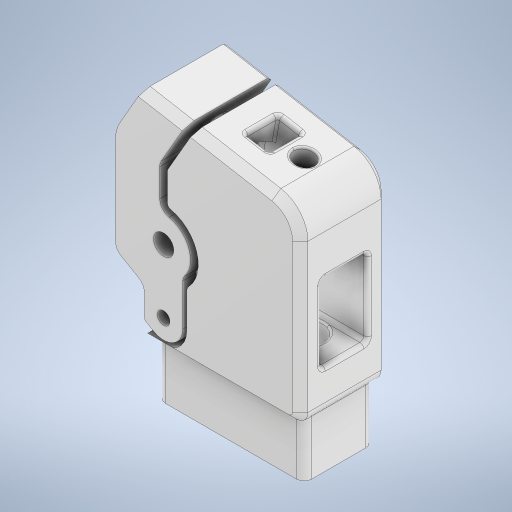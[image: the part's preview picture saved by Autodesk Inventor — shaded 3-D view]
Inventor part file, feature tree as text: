
AUTODESK INVENTOR PART (.ipt)
format: ipt  version: 2024 (Build 280153000, 153)  size: 1,094,656 bytes
history: native  units: mm
features: sketch x21, extrude x19, fillet x19, projected_geometry x14, plane x9, hole x5, other x3, mirror x3, chamfer x2
ambient origin geometry x8: Origin, YZ Plane, XZ Plane, XY Plane, X Axis, Y Axis, Z Axis, Center Point
bodies: Body1 (feature_tree), Body2 (feature_tree)
feature tree (95):
  other  "Idler Base"
  extrude  "Extrusion1"  Depth=48.0mm
  extrude  "Extrusion9"  Depth=35.0mm
  fillet  "Fillet16"  Radius=19.198622mm
  plane  "Work Plane6"
  sketch  "Sketch4"  dims[d2=31.0mm d3=35.0mm d4=19.198622mm]
  extrude  "Extrusion4"  Depth=23.0mm TaperAngle=0.0deg
  sketch  "Sketch13"  dims[d25=16.0mm d26=0.0mm d110=25.0mm]
  extrude  "Extrusion11"  Depth=25.0mm
  extrude  "Extrusion12"  TaperAngle=0.0deg  [1 undecoded]
  fillet  "Fillet17"  [1 undecoded]
  plane  "Work Plane7"
  extrude  "Extrusion13"  Depth=23.0mm
  mirror  "Mirror2"
  extrude  "Extrusion14"  Depth=10.0mm
  fillet  "Fillet18"  Radius=10.0mm
  fillet  "Fillet19"  Radius=2.0mm
  chamfer  "Chamfer5"  Distance=10.0mm
  fillet  "Fillet20"  [1 undecoded]
  hole  "Hole7"  [1 undecoded]
  extrude  "Extrusion16"  TaperAngle=0.0deg  [1 undecoded]
  fillet  "Fillet21"  Radius=2.0mm
  extrude  "Extrusion17"  Depth=1.0mm TaperAngle=45.0deg
  hole  "Hole8"  [1 undecoded]
  extrude  "Extrusion18"  Depth=2.0mm
  fillet  "Fillet22"  Radius=5.7mm
  mirror  "Mirror3"
  extrude  "Extrusion19"  Depth=8.0mm
  fillet  "Fillet23"  Radius=0.5mm
  extrude  "Extrusion20"  Depth=1.0mm
  plane  "Work Plane9"
  sketch  "Sketch26"  dims[d150=1.0mm d151=2.0mm d152=2.0mm d153=45.0deg]
  extrude  "Extrusion21"  Depth=10.5mm
  fillet  "Fillet24"  Radius=8.2mm
  fillet  "Fillet27"  Radius=5.0mm
  hole  "Hole9"  [1 undecoded]
  plane  "Work Plane11"
  plane  "Work Plane10"
  hole  "Hole10"  [1 undecoded]
  extrude  "Extrusion23"  Depth=10.5mm
  fillet  "Fillet32"  Radius=9.0mm
  extrude  "Extrusion22"  Depth=10.5mm
  fillet  "Fillet28"  Radius=1.5mm
  chamfer  "Chamfer6"  Distance=38.0mm
  mirror  "Mirror4"
  fillet  "Fillet30"  Radius=5.0mm
  fillet  "Fillet31"  Radius=2.0mm
  fillet  "Fillet33"  Radius=0.5mm
  fillet  "Fillet34"  Radius=2.0mm
  fillet  "Fillet35"  Radius=3.0mm
  plane  "Work Plane13"
  extrude  "Extrusion24"  Depth=10.5mm TaperAngle=45.0deg
  extrude  "Extrusion25"  [1 undecoded]
  hole  "Hole11"  [1 undecoded]
  fillet  "Fillet36"  Radius=0.5mm
  fillet  "Fillet37"  [1 undecoded]
  plane  "Work Plane14"
  sketch  "Sketch33"  dims[d181=2.0mm d182=0.0mm d183=2.0mm d184=8.2mm d185=5.0mm d186=0.0mm d187=120.0deg d188=20.0mm d189=18.0mm d190=9.0mm d191=38.0mm d192=1.5mm d193=0.0mm d194=38.0mm d195=5.0mm d196=0.0mm d197=2.0mm d200=0.5mm d202=2.0mm d203=0.0mm d204=3.0mm d205=2.0mm d206=2.0mm d207=45.0deg d209=5.3mm d210=6.0mm d211=4.0mm d212=2.0mm d213=90.0deg d214=8.0mm d215=0.0mm d216=-10.0mm d217=9.5mm d218=6.0mm d219=4.0mm d220=2.0mm d221=90.0deg d222=8.0mm d223=0.0mm d224=1.0mm d225=0.5mm d226=-45.0mm d227=12.0mm d228=20.0mm d229=0.0mm d230=0.5mm d231=4.0mm d232=1.0mm d233=1.0mm d234=0.5mm d235=90.0deg d236=18.0mm d237=8.25mm d238=9.0mm d239=8.0mm d240=0.0mm d241=6.0mm d242=0.0mm d243=0.5mm d244=1.0mm d245=5.4mm d246=10.0mm d247=4.0mm d248=2.0mm d249=90.0deg d250=8.0mm d251=0.0mm d252=-19.0mm d253=3.0mm d254=0.0mm d255=0.0mm d256=10.5mm d257=0.0mm d258=0.0mm]
  extrude  "Extrusion26"  Depth=10.5mm
  extrude  "Extrusion27"  Depth=10.5mm TaperAngle=0.0deg
  sketch  "Sketch1"  dims[d0=48.0mm d1=48.0mm]
  sketch  "Sketch12"  dims[d5=150.0deg d6=23.0mm d7=0.0mm]
  projected_geometry  "Projected Loop5"
  sketch  "Sketch15"  dims[d111=5.0mm d112=0.0mm d113=0.0mm d114=120.0deg]
  other  "Idler Tension Arm"
  sketch  "Sketch16"  dims[d115=3.0mm d116=23.0mm]
  projected_geometry  "Projected Loop8"
  projected_geometry  "Projected Loop10"
  sketch  "Sketch18"  dims[d117=-11.5mm d121=14.0mm d122=10.0mm d125=2.0mm]
  sketch  "Sketch19"  dims[d126=2.0mm]
  projected_geometry  "Projected Loop11"
  sketch  "Sketch20"  dims[d130=1.0mm]
  projected_geometry  "Projected Loop12"
  sketch  "Sketch22"  dims[d131=1.0mm]
  sketch  "Sketch23"  dims[d133=1.0mm d137=10.0mm d138=0.0mm d139=0.0mm d140=0.0mm]
  projected_geometry  "Projected Loop14"
  sketch  "Sketch24"  dims[d141=2.0mm d142=0.25mm]
  projected_geometry  "Projected Loop15"
  sketch  "Sketch25"  dims[d143=10.0mm d144=0.0mm d145=0.0mm d146=0.0mm d149=2.0mm]
  projected_geometry  "Projected Loop16"
  other  "Work Axis1"
  plane  "Work Plane8"
  sketch  "Sketch27"  dims[d154=2.0mm]
  sketch  "Sketch28"  dims[d155=3.3mm d156=6.0mm d157=4.0mm d158=2.0mm d159=90.0deg d160=12.0mm d161=0.0mm d162=9.0mm]
  sketch  "Sketch29"  dims[d163=2.0mm d164=0.0mm d165=2.0mm d166=5.7mm]
  plane  "Work Plane12"
  sketch  "Sketch30"  dims[d167=3.5mm d168=0.0mm]
  sketch  "Sketch31"  dims[d169=5.3mm d170=6.0mm d171=4.0mm d172=2.0mm d173=90.0deg d174=8.0mm d175=0.0mm d176=8.0mm d177=0.5mm d178=0.0mm]
  sketch  "Sketch32"  dims[d179=1.0mm d180=13.0mm]
  projected_geometry  "Project Cut Edges1"
  projected_geometry  "Project Cut Edges2"
  projected_geometry  "Project Cut Edges3"
  projected_geometry  "Project Cut Edges4"
  projected_geometry  "Project Cut Edges5"
  projected_geometry  "Project Cut Edges6"
note: 11 required parameter values undecoded (feature->parameter linkage not recoverable at this tier; creation-order binding heuristic only, values carry confidence <= 0.55)
